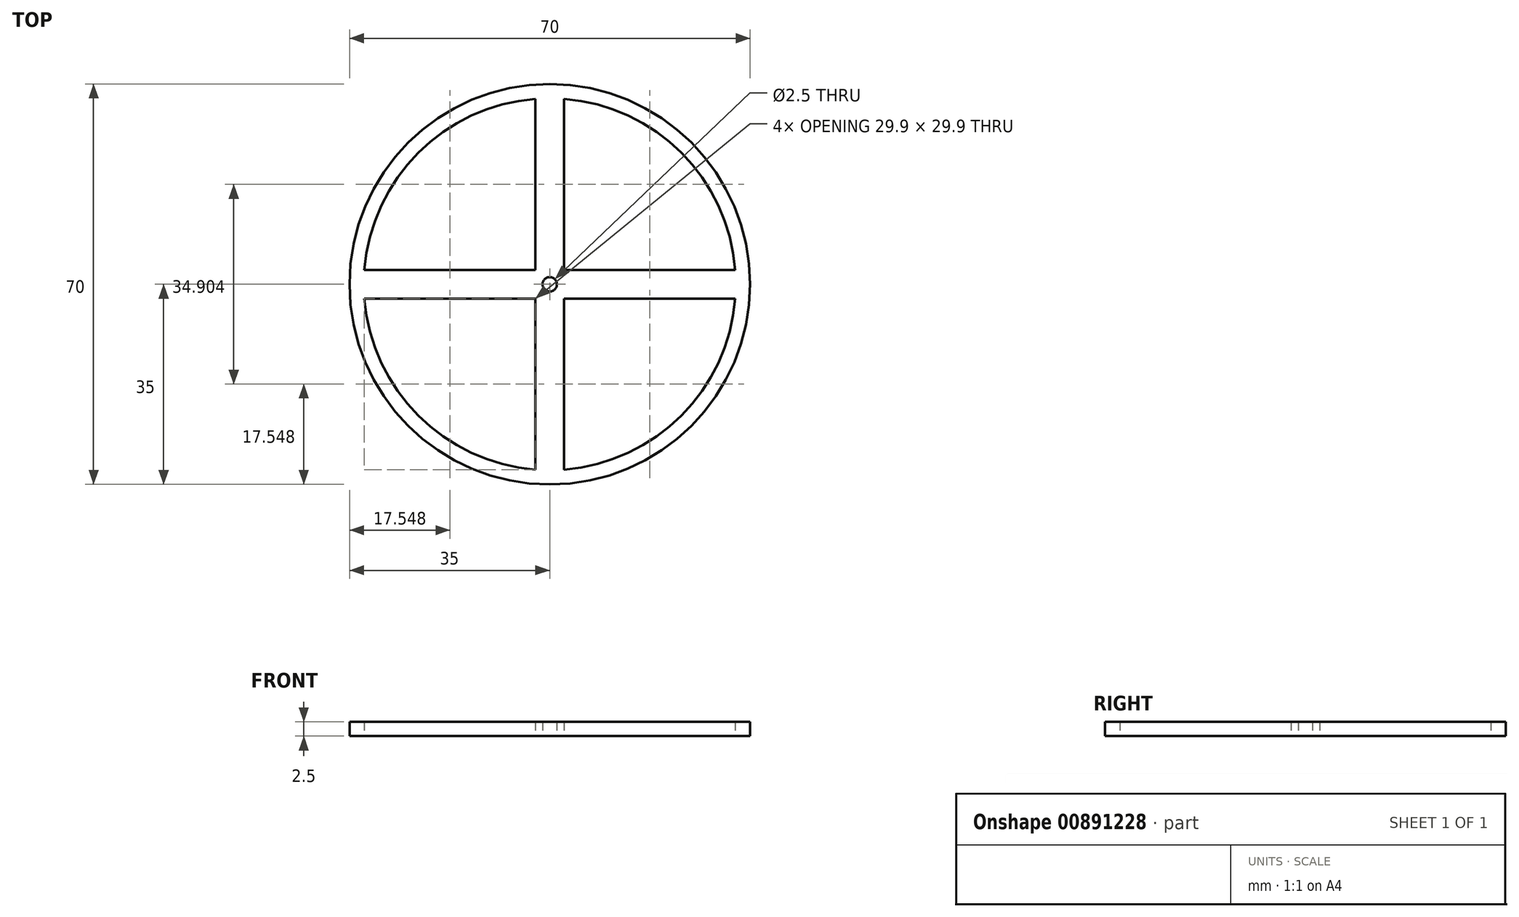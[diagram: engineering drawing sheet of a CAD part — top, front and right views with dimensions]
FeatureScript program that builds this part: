
annotation { "Feature Type Name" : "Feature", "Feature Type Description" : "" }
export const myFeature = defineFeature(function(context is Context, id is Id, definition is map)
    precondition{}
    {
        {
            var Q0;
            Q0=qCreatedBy(makeId("Top.planeOp"),FACE);
            var sketch = newSketch(context, id + "F0", { "sketchPlane" : qUnion([Q0])});
            skCircle(sketch, "E0", {"center": v(0, 0) * mm, "radius": 35 * mm});
            skArc(sketch, "E1", {"start": v(32.4, 2.5) * mm, "mid": v(22.98, 22.98) * mm, "end": v(2.5, 32.4) * mm});
            skLineSegment(sketch, "E2.bottom", {"start": v(32.4, 2.5) * mm, "end": v(2.5, 2.5) * mm});
            skLineSegment(sketch, "E2.top", {"start": v(32.4, -2.5) * mm, "end": v(2.5, -2.5) * mm});
            skPoint(sketch, "E2.left.start.orphan", {"position": v(50.2, 2.5) * mm});
            skPoint(sketch, "E3.orphan", {"position": v(50.2, -2.5) * mm});
            skArc(sketch, "E4.trimOffspring", {"start": v(-2.5, 32.4) * mm, "mid": v(-22.98, 22.98) * mm, "end": v(-32.4, 2.5) * mm});
            skLineSegment(sketch, "E5.trimOffspring", {"start": v(2.5, 32.4) * mm, "end": v(2.5, 2.5) * mm});
            skLineSegment(sketch, "E6.trimOffspring", {"start": v(-2.5, 32.4) * mm, "end": v(-2.5, 2.5) * mm});
            skArc(sketch, "E7.trimOffspring", {"start": v(-32.4, -2.5) * mm, "mid": v(-22.98, -22.98) * mm, "end": v(-2.5, -32.4) * mm});
            skArc(sketch, "E8.trimOffspring", {"start": v(2.5, -32.4) * mm, "mid": v(22.98, -22.98) * mm, "end": v(32.4, -2.5) * mm});
            skPoint(sketch, "E9.top.start.orphan", {"position": v(6.07, -46.04) * mm});
            skPoint(sketch, "E10.trimOffspring.end.orphan", {"position": v(-6.07, -46.04) * mm});
            skPoint(sketch, "E2.right.end.orphan", {"position": v(-50.2, -2.5) * mm});
            skPoint(sketch, "E11.trimOffspring.end.orphan", {"position": v(-50.2, 2.5) * mm});
            skPoint(sketch, "E9.bottom.end.orphan", {"position": v(-6.07, 46.04) * mm});
            skPoint(sketch, "E9.left.start.orphan", {"position": v(6.07, 46.04) * mm});
            skLineSegment(sketch, "E12.trimOffspring", {"start": v(-2.5, 2.5) * mm, "end": v(-32.4, 2.5) * mm});
            skLineSegment(sketch, "E13.trimOffspring", {"start": v(-2.5, -2.5) * mm, "end": v(-2.5, -32.4) * mm});
            skLineSegment(sketch, "E14.trimOffspring", {"start": v(-2.5, -2.5) * mm, "end": v(-32.4, -2.5) * mm});
            skLineSegment(sketch, "E15.trimOffspring", {"start": v(2.5, -2.5) * mm, "end": v(2.5, -32.4) * mm});
            skCircle(sketch, "E16", {"center": v(0, 0) * mm, "radius": 1.25 * mm});
            skSolve(sketch);
        }
        {
            var Q0;
            Q0 = qSketchRegion(id + "F0", true);
            extrude(context, id + "F1", {"entities" : qUnion([Q0]), "depth" : 2.5 * mm, "offsetDistance" : 25 * mm});
        }
    });
